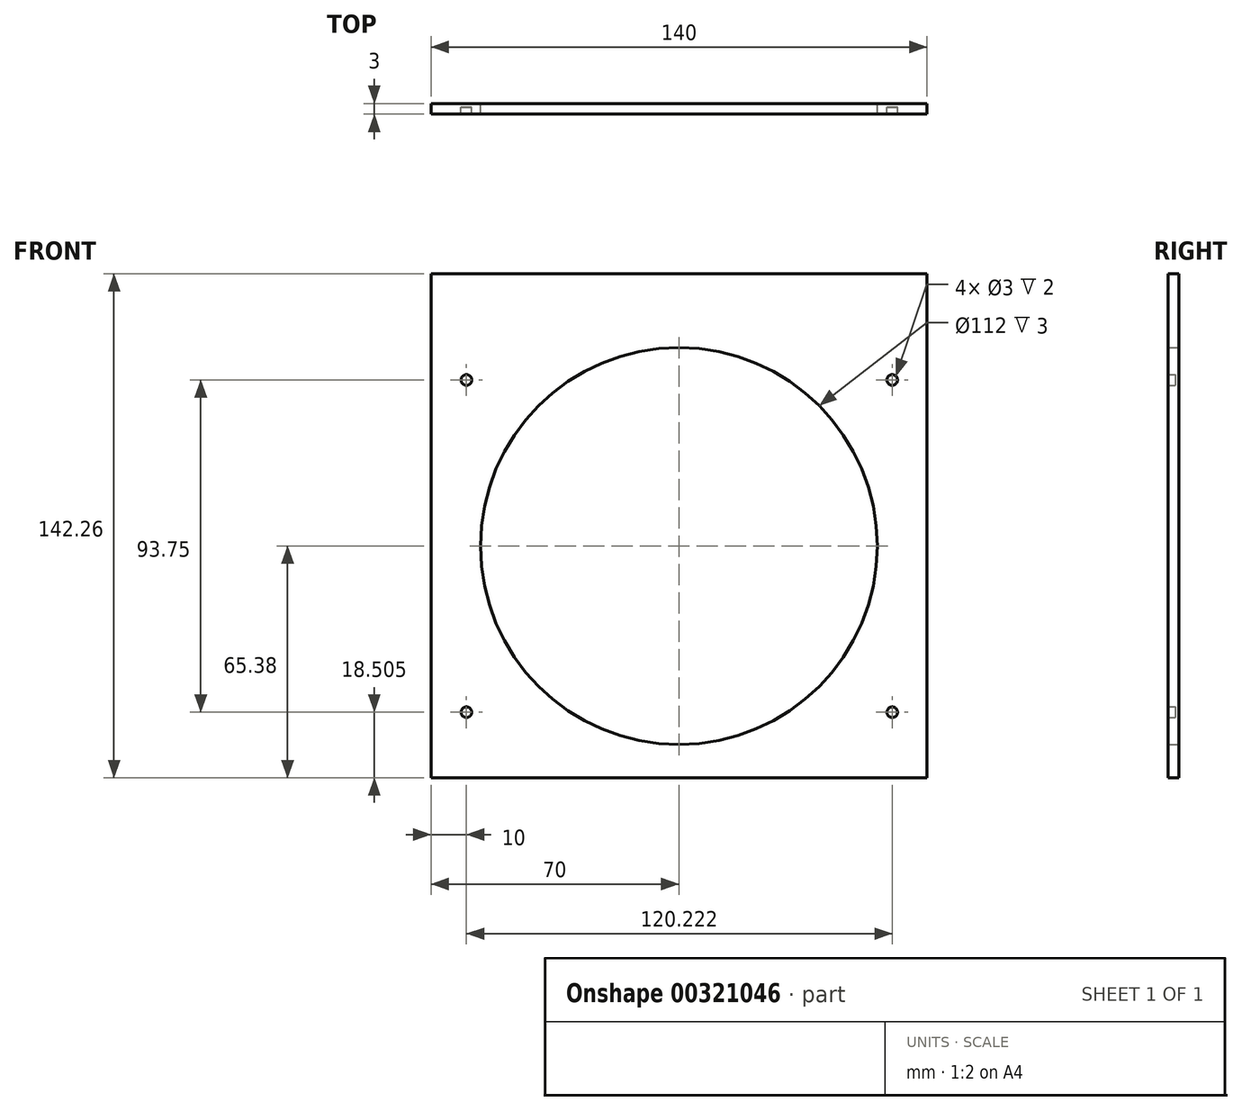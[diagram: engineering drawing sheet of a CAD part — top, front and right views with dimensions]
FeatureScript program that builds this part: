
annotation { "Feature Type Name" : "Feature", "Feature Type Description" : "" }
export const myFeature = defineFeature(function(context is Context, id is Id, definition is map)
    precondition{}
    {
        {
            var Q0;
            Q0=qCreatedBy(makeId("Front.planeOp"),FACE);
            var sketch = newSketch(context, id + "F0", { "sketchPlane" : qUnion([Q0])});
            skLineSegment(sketch, "E0.bottom", {"start": v(70, 65.38) * mm, "end": v(-70, 65.38) * mm});
            skLineSegment(sketch, "E0.top", {"start": v(70, -65.38) * mm, "end": v(-70, -65.38) * mm});
            skLineSegment(sketch, "E0.left", {"start": v(70, 65.38) * mm, "end": v(70, -65.38) * mm});
            skLineSegment(sketch, "E0.right", {"start": v(-70, 65.38) * mm, "end": v(-70, -65.38) * mm});
            skPoint(sketch, "E0.middle", {"position": v(0, 0) * mm});
            skCircle(sketch, "E1", {"center": v(0, 0) * mm, "radius": 56 * mm});
            skSolve(sketch);
        }
        {
            var Q0;
            Q0 = qSketchRegion(id + "F0", true);
            extrude(context, id + "F1", {"entities" : qUnion([Q0]), "depth" : 3 * mm});
        }
        {
            var Q0;
            Q0=makeQuery(id+"F1.opExtrude","CAP_FACE",FACE,{"disambiguationData":[OSD([sQuery(id+"F0.wireOp",EDGE,"E0.bottom"),sQuery(id+"F0.wireOp",EDGE,"E0.top"),sQuery(id+"F0.wireOp",EDGE,"E0.left"),sQuery(id+"F0.wireOp",EDGE,"E0.right"),sQuery(id+"F0.wireOp",EDGE,"E1")])],"isStart":true});
            var sketch = newSketch(context, id + "F2", { "sketchPlane" : qUnion([Q0])});
            skCircle(sketch, "E2", {"center": v(-60.22, 46.88) * mm, "radius": 1.5 * mm});
            skCircle(sketch, "E3", {"center": v(60, 46.88) * mm, "radius": 1.5 * mm});
            skCircle(sketch, "E4", {"center": v(60, -46.88) * mm, "radius": 1.5 * mm});
            skCircle(sketch, "E5", {"center": v(-60.22, -46.88) * mm, "radius": 1.5 * mm});
            skSolve(sketch);
        }
        {
            var Q0;
            Q0 = qSketchRegion(id + "F2", true);
            extrude(context, id + "F3", {"entities" : qUnion([Q0]), "operationType" : NewBodyOperationType.REMOVE, "oppositeDirection" : true, "depth" : 30 * mm});
        }
        {
            var Q0;
            Q0=makeQuery(id+"F1.opExtrude","CAP_FACE",FACE,{"disambiguationData":[OSD([sQuery(id+"F0.wireOp",EDGE,"E0.bottom"),sQuery(id+"F0.wireOp",EDGE,"E0.top"),sQuery(id+"F0.wireOp",EDGE,"E0.left"),sQuery(id+"F0.wireOp",EDGE,"E0.right"),sQuery(id+"F0.wireOp",EDGE,"E1")])],"isStart":true});
            var sketch = newSketch(context, id + "F4", { "sketchPlane" : qUnion([Q0])});
            skLineSegment(sketch, "E6.bottom", {"start": v(-50.17, 52.19) * mm, "end": v(-65.7, 52.19) * mm});
            skLineSegment(sketch, "E6.top", {"start": v(-50.17, 39.6) * mm, "end": v(-65.7, 39.6) * mm});
            skLineSegment(sketch, "E6.left", {"start": v(-50.17, 52.19) * mm, "end": v(-50.17, 39.6) * mm});
            skLineSegment(sketch, "E6.right", {"start": v(-65.7, 52.19) * mm, "end": v(-65.7, 39.6) * mm});
            skLineSegment(sketch, "E7.bottom", {"start": v(-53.12, -44.73) * mm, "end": v(-65.08, -44.73) * mm});
            skLineSegment(sketch, "E7.top", {"start": v(-53.12, -50.8) * mm, "end": v(-65.08, -50.8) * mm});
            skLineSegment(sketch, "E7.left", {"start": v(-53.12, -44.73) * mm, "end": v(-53.12, -50.8) * mm});
            skLineSegment(sketch, "E7.right", {"start": v(-65.08, -44.73) * mm, "end": v(-65.08, -50.8) * mm});
            skLineSegment(sketch, "E8.bottom", {"start": v(52.66, -53.12) * mm, "end": v(63.84, -53.12) * mm});
            skLineSegment(sketch, "E8.top", {"start": v(52.66, -40.85) * mm, "end": v(63.84, -40.85) * mm});
            skLineSegment(sketch, "E8.left", {"start": v(52.66, -53.12) * mm, "end": v(52.66, -40.85) * mm});
            skLineSegment(sketch, "E8.right", {"start": v(63.84, -53.12) * mm, "end": v(63.84, -40.85) * mm});
            skLineSegment(sketch, "E9.bottom", {"start": v(54.83, 42.1) * mm, "end": v(64.77, 42.1) * mm});
            skLineSegment(sketch, "E9.top", {"start": v(54.83, 51.1) * mm, "end": v(64.77, 51.1) * mm});
            skLineSegment(sketch, "E9.left", {"start": v(54.83, 42.1) * mm, "end": v(54.83, 51.1) * mm});
            skLineSegment(sketch, "E9.right", {"start": v(64.77, 42.1) * mm, "end": v(64.77, 51.1) * mm});
            skSolve(sketch);
        }
        {
            var Q0;
            Q0 = qSketchRegion(id + "F4", true);
            extrude(context, id + "F5", {"entities" : qUnion([Q0]), "operationType" : NewBodyOperationType.ADD, "oppositeDirection" : true, "depth" : 1 * mm});
        }
        {
            var Q0;
            Q0=makeQuery(id+"F1.opExtrude","SWEPT_FACE",FACE,{"disambiguationData":[OSD([sQuery(id+"F0.wireOp",EDGE,"E0.bottom")])]});
            var sketch = newSketch(context, id + "F6", { "sketchPlane" : qUnion([Q0])});
            skLineSegment(sketch, "E10.bottom", {"start": v(-70, 0) * mm, "end": v(70, 0) * mm});
            skLineSegment(sketch, "E10.top", {"start": v(-70, -3) * mm, "end": v(70, -3) * mm});
            skLineSegment(sketch, "E10.left", {"start": v(-70, 0) * mm, "end": v(-70, -3) * mm});
            skLineSegment(sketch, "E10.right", {"start": v(70, 0) * mm, "end": v(70, -3) * mm});
            skSolve(sketch);
        }
        {
            var Q0;
            Q0 = qSketchRegion(id + "F6", true);
            extrude(context, id + "F7", {"entities" : qUnion([Q0]), "operationType" : NewBodyOperationType.ADD, "depth" : 11.5 * mm});
        }
    });
